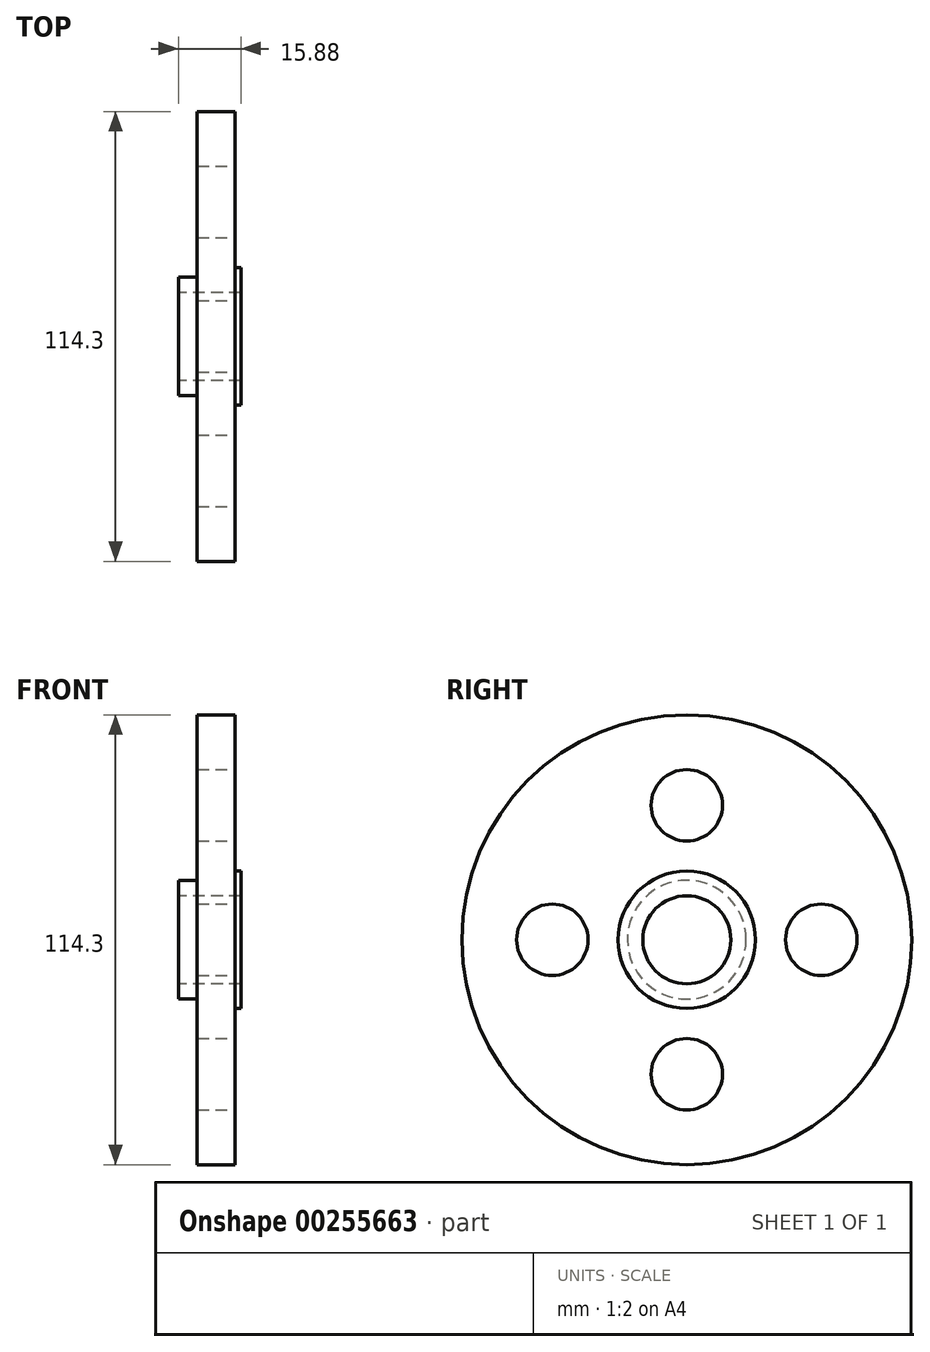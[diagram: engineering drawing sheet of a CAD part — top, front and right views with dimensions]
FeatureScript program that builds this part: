
annotation { "Feature Type Name" : "Feature", "Feature Type Description" : "" }
export const myFeature = defineFeature(function(context is Context, id is Id, definition is map)
    precondition{}
    {
        {
            var Q0;
            Q0=qCreatedBy(makeId("Front.planeOp"),FACE);
            var sketch = newSketch(context, id + "F0", { "sketchPlane" : qUnion([Q0])});
            skLineSegment(sketch, "E0", {"start": v(-25.36, 0) * mm, "end": v(28.82, 0) * mm, "construction": true});
            skLineSegment(sketch, "E1", {"start": v(0, 11.18) * mm, "end": v(15.88, 11.18) * mm});
            skLineSegment(sketch, "E2", {"start": v(15.88, 11.18) * mm, "end": v(15.88, 17.46) * mm});
            skLineSegment(sketch, "E3", {"start": v(15.88, 17.46) * mm, "end": v(14.35, 17.46) * mm});
            skLineSegment(sketch, "E4", {"start": v(14.35, 17.46) * mm, "end": v(14.35, 57.15) * mm});
            skLineSegment(sketch, "E5", {"start": v(14.35, 57.15) * mm, "end": v(4.78, 57.15) * mm});
            skLineSegment(sketch, "E6", {"start": v(4.78, 57.15) * mm, "end": v(4.78, 15.09) * mm});
            skLineSegment(sketch, "E7", {"start": v(4.78, 15.09) * mm, "end": v(0, 15.09) * mm});
            skLineSegment(sketch, "E8", {"start": v(0, 15.09) * mm, "end": v(0, 11.18) * mm});
            skSolve(sketch);
        }
        {
            var Q0;
            Q0 = qSketchRegion(id + "F0", true);
            var Q1;
            Q1=sQuery(id+"F0.wireOp",EDGE,"E0");
            revolve(context, id + "F1", {"entities" : qUnion([Q0]), "axis" : qUnion([Q1]), "revolveType" : RevolveType.FULL});
        }
        {
            var Q0;
            Q0=makeQuery(id+"F1.opRevolve","SWEPT_FACE",FACE,{"disambiguationData":[OSD([sQuery(id+"F0.wireOp",EDGE,"E4")])]});
            var sketch = newSketch(context, id + "F2", { "sketchPlane" : qUnion([Q0])});
            skCircle(sketch, "E9", {"center": v(0, 0) * mm, "radius": 34.16 * mm, "construction": true});
            skCircle(sketch, "E10", {"center": v(0, 34.16) * mm, "radius": 9.07 * mm});
            skCircle(sketch, "E11.1.0", {"center": v(-34.16, 0) * mm, "radius": 9.07 * mm});
            skCircle(sketch, "E11.2.0", {"center": v(0, -34.16) * mm, "radius": 9.07 * mm});
            skCircle(sketch, "E11.3.0", {"center": v(34.16, 0) * mm, "radius": 9.07 * mm});
            skSolve(sketch);
        }
        {
            var Q0;
            Q0=makeQuery(id+"F2.imprint","IMPRINT",FACE,{"disambiguationData":[TD([[makeQuery(id+"F2.imprint","IMPRINT",EDGE,{"derivedFrom":sQuery(id+"F2.wireOp",EDGE,"E11.1.0")}),1.0]])]});
            var Q1;
            Q1=makeQuery(id+"F2.imprint","IMPRINT",FACE,{"disambiguationData":[TD([[makeQuery(id+"F2.imprint","IMPRINT",EDGE,{"derivedFrom":sQuery(id+"F2.wireOp",EDGE,"E11.2.0")}),1.0]])]});
            var Q2;
            Q2=makeQuery(id+"F2.imprint","IMPRINT",FACE,{"disambiguationData":[TD([[makeQuery(id+"F2.imprint","IMPRINT",EDGE,{"derivedFrom":sQuery(id+"F2.wireOp",EDGE,"E11.3.0")}),1.0]])]});
            var Q3;
            Q3=makeQuery(id+"F2.imprint","IMPRINT",FACE,{"disambiguationData":[TD([[makeQuery(id+"F2.imprint","IMPRINT",EDGE,{"derivedFrom":sQuery(id+"F2.wireOp",EDGE,"E10")}),1.0]])]});
            extrude(context, id + "F3", {"entities" : qUnion([Q0, Q1, Q2, Q3]), "operationType" : NewBodyOperationType.REMOVE, "endBound" : BoundingType.THROUGH_ALL, "oppositeDirection" : true, "depth" : 25.4 * mm});
        }
    });
